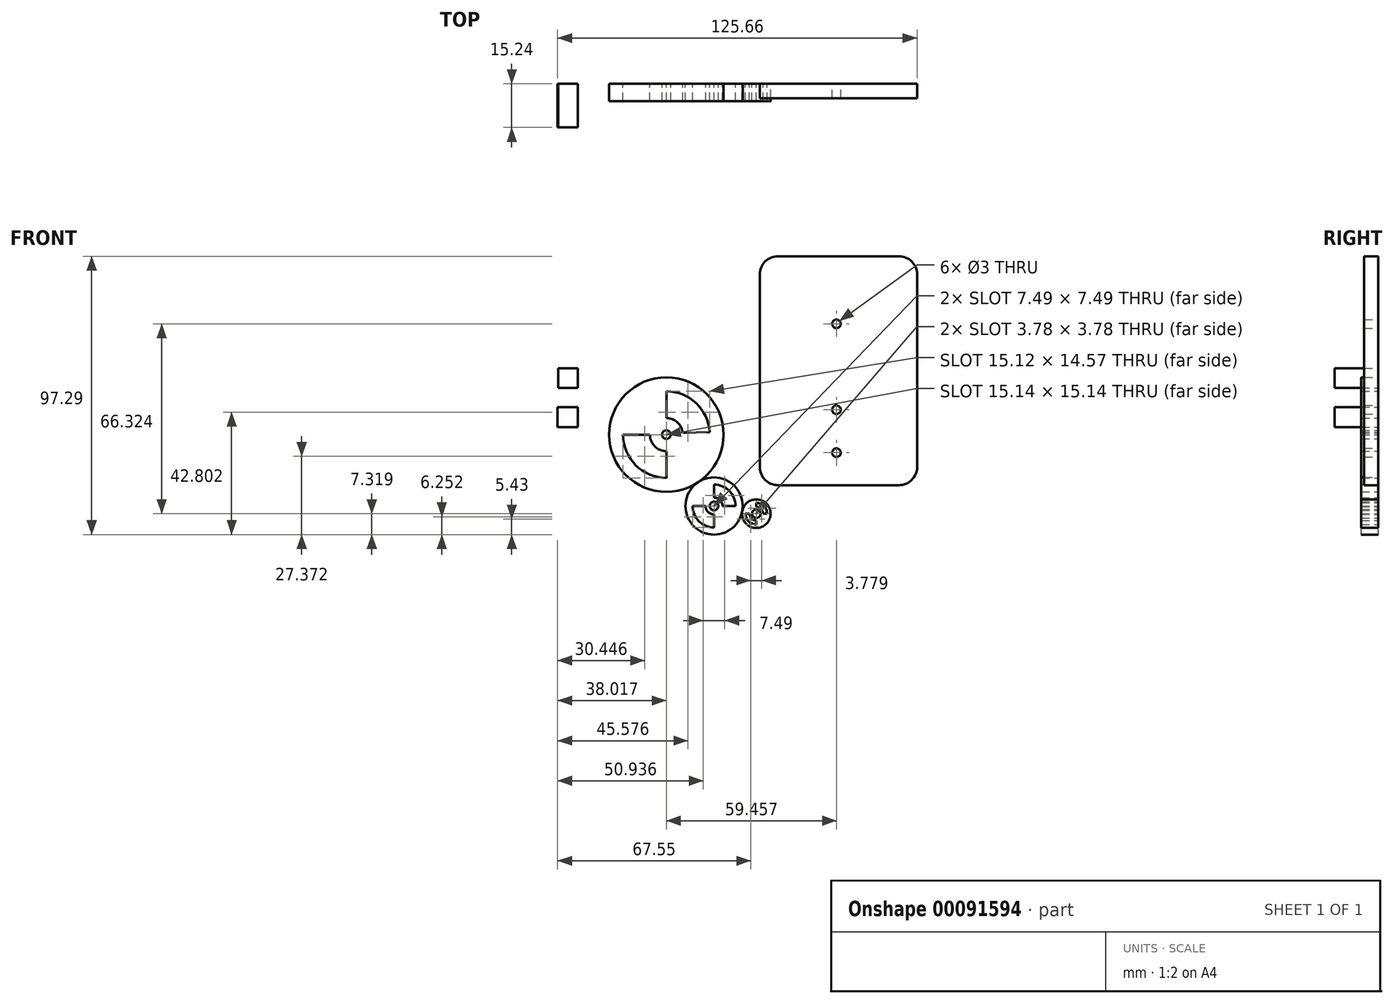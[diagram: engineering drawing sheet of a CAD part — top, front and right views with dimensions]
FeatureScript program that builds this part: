
annotation { "Feature Type Name" : "Feature", "Feature Type Description" : "" }
export const myFeature = defineFeature(function(context is Context, id is Id, definition is map)
    precondition{}
    {
        {
            var Q0;
            Q0=qCreatedBy(makeId("Front.planeOp"),FACE);
            var sketch = newSketch(context, id + "F0", { "sketchPlane" : qUnion([Q0])});
            skCircle(sketch, "E0", {"center": v(-26.88, 12.18) * mm, "radius": 20 * mm});
            skCircle(sketch, "E1", {"center": v(-10.22, -12.76) * mm, "radius": 10 * mm});
            skCircle(sketch, "E2", {"center": v(4.54, -15.44) * mm, "radius": 5 * mm});
            skPoint(sketch, "E3.visualSharp", {"position": v(-55, 40) * mm});
            skPoint(sketch, "E4.visualSharp", {"position": v(0, 40) * mm});
            skPoint(sketch, "E5.visualSharp", {"position": v(-55, -30) * mm});
            skPoint(sketch, "E6.visualSharp", {"position": v(22.5, -30) * mm});
            skPoint(sketch, "E7.visualSharp", {"position": v(22.5, 0) * mm});
            skPoint(sketch, "E8.visualSharp", {"position": v(0, 0) * mm});
            skPoint(sketch, "E9.end.orphan", {"position": v(0, -30) * mm});
            skArc(sketch, "E10", {"start": v(-32.65, 12.18) * mm, "mid": v(-30.96, 8.1) * mm, "end": v(-26.88, 6.41) * mm});
            skArc(sketch, "E11", {"start": v(-42.03, 12.18) * mm, "mid": v(-37.6, 1.48) * mm, "end": v(-26.88, -2.96) * mm});
            skArc(sketch, "E12", {"start": v(-13.17, -12.76) * mm, "mid": v(-12.3, -14.85) * mm, "end": v(-10.22, -15.72) * mm});
            skArc(sketch, "E13", {"start": v(-17.7, -12.76) * mm, "mid": v(-15.52, -18.06) * mm, "end": v(-10.22, -20.25) * mm});
            skArc(sketch, "E14", {"start": v(2.16, -15.44) * mm, "mid": v(2.86, -17.12) * mm, "end": v(4.54, -17.82) * mm});
            skArc(sketch, "E15", {"start": v(0.76, -15.44) * mm, "mid": v(1.87, -18.11) * mm, "end": v(4.54, -19.22) * mm});
            skLineSegment(sketch, "E16", {"start": v(-26.88, 27.33) * mm, "end": v(-26.88, 17.95) * mm});
            skLineSegment(sketch, "E17", {"start": v(-42.03, 12.18) * mm, "end": v(-32.65, 12.18) * mm});
            skLineSegment(sketch, "E18.trimOffspring", {"start": v(-26.88, 6.41) * mm, "end": v(-26.88, -2.96) * mm});
            skLineSegment(sketch, "E19.trimOffspring", {"start": v(-32.65, 12.18) * mm, "end": v(-42.03, 12.18) * mm});
            skLineSegment(sketch, "E20.trimOffspring", {"start": v(-26.88, 17.95) * mm, "end": v(-26.88, 27.33) * mm});
            skLineSegment(sketch, "E21.trimOffspring", {"start": v(-21.14, 12.76) * mm, "end": v(-11.76, 13.02) * mm});
            skArc(sketch, "E22.trimOffspring", {"start": v(-11.76, 13.02) * mm, "mid": v(-16.48, 23.18) * mm, "end": v(-26.88, 27.33) * mm});
            skArc(sketch, "E23.trimOffspring", {"start": v(-21.14, 12.76) * mm, "mid": v(-23.01, 16.46) * mm, "end": v(-26.88, 17.95) * mm});
            skPoint(sketch, "E24.end.orphan", {"position": v(-25.64, 13.02) * mm});
            skLineSegment(sketch, "E25", {"start": v(-10.22, -20.25) * mm, "end": v(-10.22, -15.72) * mm});
            skLineSegment(sketch, "E26.trimOffspring", {"start": v(-10.22, -15.72) * mm, "end": v(-10.22, -20.25) * mm});
            skLineSegment(sketch, "E27.trimOffspring", {"start": v(-10.22, -9.8) * mm, "end": v(-10.22, -5.27) * mm});
            skLineSegment(sketch, "E28", {"start": v(-13.17, -12.76) * mm, "end": v(-17.7, -12.76) * mm});
            skLineSegment(sketch, "E29", {"start": v(-17.7, -12.76) * mm, "end": v(-13.17, -12.76) * mm});
            skLineSegment(sketch, "E30.trimOffspring", {"start": v(-7.26, -12.76) * mm, "end": v(-2.73, -12.76) * mm});
            skArc(sketch, "E31.trimOffspring", {"start": v(-2.73, -12.76) * mm, "mid": v(-4.92, -7.47) * mm, "end": v(-10.22, -5.27) * mm});
            skArc(sketch, "E32.trimOffspring", {"start": v(-7.26, -12.76) * mm, "mid": v(-8.13, -10.67) * mm, "end": v(-10.22, -9.8) * mm});
            skLineSegment(sketch, "E33", {"start": v(4.54, -17.82) * mm, "end": v(4.54, -19.22) * mm});
            skLineSegment(sketch, "E34", {"start": v(4.54, -19.22) * mm, "end": v(4.54, -17.82) * mm});
            skLineSegment(sketch, "E35", {"start": v(4.54, -11.66) * mm, "end": v(4.54, -13.06) * mm});
            skLineSegment(sketch, "E36", {"start": v(6.92, -15.44) * mm, "end": v(8.32, -15.44) * mm});
            skLineSegment(sketch, "E37.trimOffspring", {"start": v(4.54, -13.06) * mm, "end": v(4.54, -11.66) * mm});
            skLineSegment(sketch, "E38.trimOffspring", {"start": v(2.16, -15.44) * mm, "end": v(0.76, -15.44) * mm});
            skArc(sketch, "E39.trimOffspring", {"start": v(6.92, -15.44) * mm, "mid": v(6.22, -13.76) * mm, "end": v(4.54, -13.06) * mm});
            skArc(sketch, "E40.trimOffspring", {"start": v(8.32, -15.44) * mm, "mid": v(7.21, -12.77) * mm, "end": v(4.54, -11.66) * mm});
            skCircle(sketch, "E41", {"center": v(-26.88, 12.18) * mm, "radius": 1.5 * mm});
            skCircle(sketch, "E42", {"center": v(-10.22, -12.76) * mm, "radius": 1.5 * mm});
            skCircle(sketch, "E43", {"center": v(4.54, -15.44) * mm, "radius": 1.5 * mm});
            skSolve(sketch);
        }
        {
            var Q0;
            Q0=makeQuery(id+"F0.imprint","IMPRINT",FACE,{"disambiguationData":[TD([[makeQuery(id+"F0.imprint","IMPRINT",EDGE,{"derivedFrom":sQuery(id+"F0.wireOp",EDGE,"E0")}),1.0]])]});
            var Q1;
            Q1=makeQuery(id+"F0.imprint","IMPRINT",FACE,{"disambiguationData":[TD([[makeQuery(id+"F0.imprint","IMPRINT",EDGE,{"derivedFrom":sQuery(id+"F0.wireOp",EDGE,"E1")}),1.0]])]});
            var Q2;
            Q2=makeQuery(id+"F0.imprint","IMPRINT",FACE,{"disambiguationData":[TD([[makeQuery(id+"F0.imprint","IMPRINT",EDGE,{"derivedFrom":sQuery(id+"F0.wireOp",EDGE,"E2")}),1.0]])]});
            extrude(context, id + "F1", {"entities" : qUnion([Q0, Q1, Q2]), "depth" : 6 * mm});
        }
        {
            var Q0;
            Q0=qCreatedBy(makeId("Front.planeOp"),FACE);
            var sketch = newSketch(context, id + "F2", { "sketchPlane" : qUnion([Q0])});
            skLineSegment(sketch, "E44.bottom", {"start": v(12.12, 74.53) * mm, "end": v(54.41, 74.53) * mm});
            skLineSegment(sketch, "E44.top", {"start": v(12.12, -5.47) * mm, "end": v(54.41, -5.47) * mm});
            skLineSegment(sketch, "E44.left", {"start": v(5.77, 68.18) * mm, "end": v(5.77, 0.88) * mm});
            skLineSegment(sketch, "E44.right", {"start": v(60.76, 68.18) * mm, "end": v(60.76, 30.88) * mm});
            skPoint(sketch, "E45.visualSharp", {"position": v(5.77, 74.53) * mm});
            skArc(sketch, "E45.filletArc", {"start": v(12.12, 74.53) * mm, "mid": v(7.63, 72.67) * mm, "end": v(5.77, 68.18) * mm});
            skPoint(sketch, "E46.visualSharp", {"position": v(60.76, 74.53) * mm});
            skArc(sketch, "E46.filletArc", {"start": v(60.76, 68.18) * mm, "mid": v(58.9, 72.67) * mm, "end": v(54.41, 74.53) * mm});
            skPoint(sketch, "E47.visualSharp", {"position": v(5.77, -5.47) * mm});
            skArc(sketch, "E47.filletArc", {"start": v(5.77, 0.88) * mm, "mid": v(7.63, -3.6) * mm, "end": v(12.12, -5.47) * mm});
            skLineSegment(sketch, "E48", {"start": v(60.76, 30.88) * mm, "end": v(60.76, 0.88) * mm});
            skPoint(sketch, "E49.visualSharp", {"position": v(60.76, -5.47) * mm});
            skArc(sketch, "E49.filletArc", {"start": v(54.41, -5.47) * mm, "mid": v(58.9, -3.6) * mm, "end": v(60.76, 0.88) * mm});
            skCircle(sketch, "E50", {"center": v(32.57, 50.88) * mm, "radius": 1.5 * mm});
            skCircle(sketch, "E51", {"center": v(32.57, 20.88) * mm, "radius": 1.5 * mm});
            skCircle(sketch, "E52", {"center": v(32.57, 5.88) * mm, "radius": 1.5 * mm});
            skSolve(sketch);
        }
        {
            var Q0;
            Q0=makeQuery(id+"F2.imprint","IMPRINT",FACE,{"disambiguationData":[TD([[makeQuery(id+"F2.imprint","IMPRINT",EDGE,{"derivedFrom":sQuery(id+"F2.wireOp",EDGE,"E44.bottom")}),-1.0]])]});
            extrude(context, id + "F3", {"entities" : qUnion([Q0]), "depth" : 5 * mm});
        }
        {
            var Q0;
            Q0=qCreatedBy(makeId("Front.planeOp"),FACE);
            var sketch = newSketch(context, id + "F4", { "sketchPlane" : qUnion([Q0])});
            skLineSegment(sketch, "E53.bottom", {"start": v(-64.9, 21.76) * mm, "end": v(-57.88, 21.76) * mm});
            skLineSegment(sketch, "E53.top", {"start": v(-64.9, 14.74) * mm, "end": v(-57.88, 14.74) * mm});
            skLineSegment(sketch, "E53.left", {"start": v(-64.9, 21.76) * mm, "end": v(-64.9, 14.74) * mm});
            skLineSegment(sketch, "E53.right", {"start": v(-57.88, 21.76) * mm, "end": v(-57.88, 14.74) * mm});
            skLineSegment(sketch, "E54.bottom", {"start": v(-64.66, 35.33) * mm, "end": v(-57.88, 35.33) * mm});
            skLineSegment(sketch, "E54.top", {"start": v(-64.66, 28.54) * mm, "end": v(-57.88, 28.54) * mm});
            skLineSegment(sketch, "E54.left", {"start": v(-64.66, 35.33) * mm, "end": v(-64.66, 28.54) * mm});
            skLineSegment(sketch, "E54.right", {"start": v(-57.88, 35.33) * mm, "end": v(-57.88, 28.54) * mm});
            skSolve(sketch);
        }
        {
            var Q0;
            Q0=makeQuery(id+"F4.imprint","IMPRINT",FACE,{"disambiguationData":[TD([[makeQuery(id+"F4.imprint","IMPRINT",EDGE,{"derivedFrom":sQuery(id+"F4.wireOp",EDGE,"E53.bottom")}),-1.0]])]});
            var Q1;
            Q1=makeQuery(id+"F4.imprint","IMPRINT",FACE,{"disambiguationData":[TD([[makeQuery(id+"F4.imprint","IMPRINT",EDGE,{"derivedFrom":sQuery(id+"F4.wireOp",EDGE,"E54.bottom")}),-1.0]])]});
            extrude(context, id + "F5", {"entities" : qUnion([Q0, Q1]), "depth" : 15.24 * mm});
        }
    });
